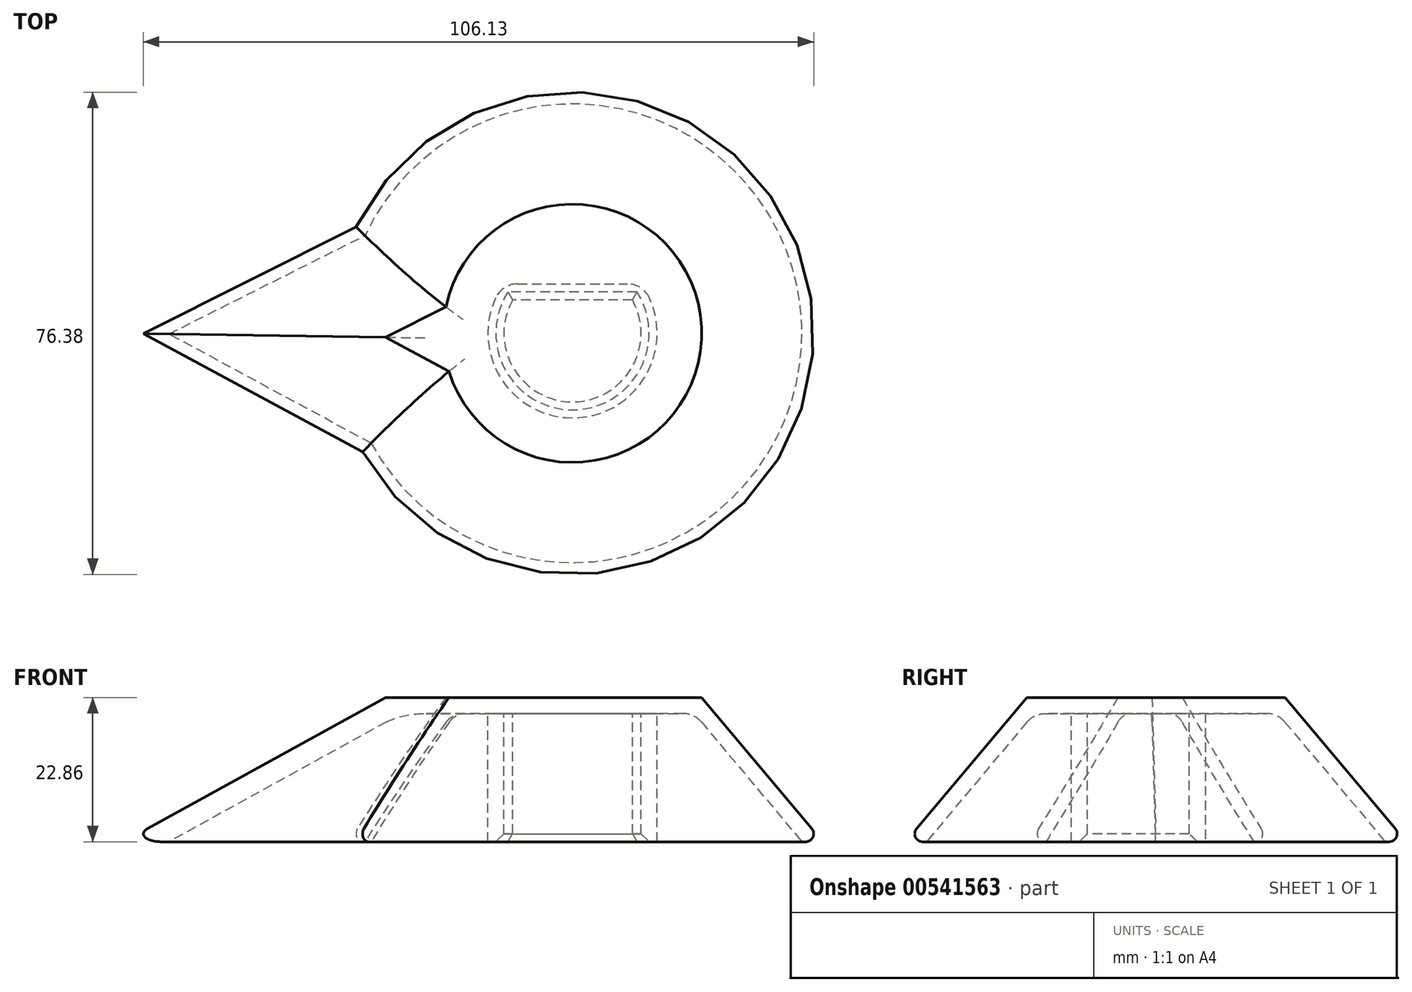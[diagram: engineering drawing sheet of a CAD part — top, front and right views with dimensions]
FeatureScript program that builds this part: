
annotation { "Feature Type Name" : "Feature", "Feature Type Description" : "" }
export const myFeature = defineFeature(function(context is Context, id is Id, definition is map)
    precondition{}
    {
        {
            var Q0;
            Q0=qCreatedBy(makeId("Top.planeOp"),FACE);
            var sketch = newSketch(context, id + "F0", { "sketchPlane" : qUnion([Q0])});
            skArc(sketch, "E0", {"start": v(-34.3, -19.87) * mm, "mid": v(39.63, 1.1) * mm, "end": v(-35.35, 17.94) * mm});
            skLineSegment(sketch, "E1", {"start": v(-35.35, 17.94) * mm, "end": v(-71.09, 0) * mm});
            skLineSegment(sketch, "E2", {"start": v(-71.09, 0) * mm, "end": v(-34.3, -19.87) * mm});
            skSolve(sketch);
        }
        {
            var Q0;
            Q0 = qSketchRegion(id + "F0", true);
            extrude(context, id + "F1", {"entities" : qUnion([Q0]), "depth" : 22.86 * mm, "offsetDistance" : 25.4 * mm, "hasDraft" : true, "draftAngle" : 40 * degree, "draftPullDirection" : true});
        }
        {
            var Q0;
            Q0=makeQuery(id+"F1.opExtrude","CAP_FACE",FACE,{"disambiguationData":[OSD([sQuery(id+"F0.wireOp",EDGE,"E0"),sQuery(id+"F0.wireOp",EDGE,"E1"),sQuery(id+"F0.wireOp",EDGE,"E2")])],"isStart":false});
            var sketch = newSketch(context, id + "F2", { "sketchPlane" : qUnion([Q0])});
            skArc(sketch, "E3", {"start": v(-9.5, 5.28) * mm, "mid": v(0, -10.86) * mm, "end": v(9.5, 5.28) * mm});
            skLineSegment(sketch, "E4", {"start": v(-9.5, 5.28) * mm, "end": v(9.5, 5.28) * mm});
            skSolve(sketch);
        }
        {
            var Q0;
            Q0 = qSketchRegion(id + "F2", true);
            extrude(context, id + "F3", {"entities" : qUnion([Q0]), "operationType" : NewBodyOperationType.REMOVE, "oppositeDirection" : true, "depth" : 47 * mm, "offsetDistance" : 25.4 * mm});
        }
        {
            var Q0;
            Q0=makeQuery(id+"F1.opExtrude","CAP_FACE",FACE,{"disambiguationData":[OSD([sQuery(id+"F0.wireOp",EDGE,"E0"),sQuery(id+"F0.wireOp",EDGE,"E1"),sQuery(id+"F0.wireOp",EDGE,"E2")])],"isStart":true});
            shell(context, id + "F4", {"entities" : qUnion([Q0]), "thickness" : 2.54 * mm});
        }
        {
            var Q0;
            Q0=makeQuery(id+"F4.opShell","OFFSET_EDGE",EDGE,{"disambiguationData":[OSD([sQuery(id+"F2.wireOp",EDGE,"E4")])]});
            var Q1;
            Q1=makeQuery(id+"F4.opShell","OFFSET_EDGE",EDGE,{"disambiguationData":[OSD([sQuery(id+"F2.wireOp",EDGE,"E3")])]});
            var Q2;
            {var subQ0=sQuery(id+"F0.wireOp",EDGE,"E0");Q2=makeQuery(id+"F4.opShell","OFFSET_EDGE",EDGE,{"disambiguationData":[OSD([subQ0]),TDD([makeQuery(id+"F1.opExtrude","CAP_EDGE",EDGE,{"disambiguationData":[OSD([subQ0])],"isStart":false})])]});}
            var Q3;
            {var subQ0=sQuery(id+"F0.wireOp",EDGE,"E1");Q3=makeQuery(id+"F4.opShell","OFFSET_EDGE",EDGE,{"disambiguationData":[OSD([subQ0]),TDD([makeQuery(id+"F1.opExtrude","CAP_EDGE",EDGE,{"disambiguationData":[OSD([subQ0])],"isStart":false})])]});}
            var Q4;
            {var subQ0=sQuery(id+"F0.wireOp",EDGE,"E2");Q4=makeQuery(id+"F4.opShell","OFFSET_EDGE",EDGE,{"disambiguationData":[OSD([subQ0]),TDD([makeQuery(id+"F1.opExtrude","CAP_EDGE",EDGE,{"disambiguationData":[OSD([subQ0])],"isStart":false})])]});}
            fillet(context, id + "F5", {"entities" : qUnion([Q0, Q1, Q2, Q3, Q4]), "radius" : 3.8 * mm, "tangentPropagation" : true, "allowEdgeOverflow" : false});
        }
        {
            var Q0;
            Q0=makeQuery(id+"F1.opExtrude","CAP_EDGE",EDGE,{"disambiguationData":[OSD([sQuery(id+"F0.wireOp",EDGE,"E0")])],"isStart":true});
            var Q1;
            Q1=makeQuery(id+"F1.opExtrude","CAP_EDGE",EDGE,{"disambiguationData":[OSD([sQuery(id+"F0.wireOp",EDGE,"E1")])],"isStart":true});
            var Q2;
            Q2=makeQuery(id+"F1.opExtrude","CAP_EDGE",EDGE,{"disambiguationData":[OSD([sQuery(id+"F0.wireOp",EDGE,"E2")])],"isStart":true});
            fillet(context, id + "F6", {"entities" : qUnion([Q0, Q1, Q2]), "radius" : 1.27 * mm, "tangentPropagation" : true, "allowEdgeOverflow" : false});
        }
        {
            var Q0;
            Q0=makeQuery(id+"F3.boolean.opBoolean","INTERSECT",EDGE,{"derivedFrom":[makeQuery(id+"F1.opExtrude","CAP_FACE",FACE,{"disambiguationData":[OSD([sQuery(id+"F0.wireOp",EDGE,"E0"),sQuery(id+"F0.wireOp",EDGE,"E1"),sQuery(id+"F0.wireOp",EDGE,"E2")])],"isStart":true}),makeQuery(id+"F3.opExtrude","SWEPT_FACE",FACE,{"disambiguationData":[OSD([sQuery(id+"F2.wireOp",EDGE,"E4")])]})]});
            var Q1;
            Q1=makeQuery(id+"F3.boolean.opBoolean","INTERSECT",EDGE,{"derivedFrom":[makeQuery(id+"F1.opExtrude","CAP_FACE",FACE,{"disambiguationData":[OSD([sQuery(id+"F0.wireOp",EDGE,"E0"),sQuery(id+"F0.wireOp",EDGE,"E1"),sQuery(id+"F0.wireOp",EDGE,"E2")])],"isStart":true}),makeQuery(id+"F3.opExtrude","SWEPT_FACE",FACE,{"disambiguationData":[OSD([sQuery(id+"F2.wireOp",EDGE,"E3")])]})]});
            chamfer(context, id + "F7", {"entities" : qUnion([Q0, Q1]), "width" : 1.27 * mm, "tangentPropagation" : true});
        }
        {
            var Q0;
            Q0=makeQuery(id+"F1.opExtrude","CAP_FACE",FACE,{"disambiguationData":[OSD([sQuery(id+"F0.wireOp",EDGE,"E0"),sQuery(id+"F0.wireOp",EDGE,"E1"),sQuery(id+"F0.wireOp",EDGE,"E2")])],"isStart":false});
            var sketch = newSketch(context, id + "F8", { "sketchPlane" : qUnion([Q0])});
            skCircle(sketch, "E5", {"center": v(0, 0) * mm, "radius": 12.56 * mm});
            skSolve(sketch);
        }
        {
            var Q0;
            Q0 = qSketchRegion(id + "F8", true);
            extrude(context, id + "F9", {"entities" : qUnion([Q0]), "operationType" : NewBodyOperationType.ADD, "oppositeDirection" : true, "depth" : 2.54 * mm, "offsetDistance" : 25.4 * mm});
        }
    });
